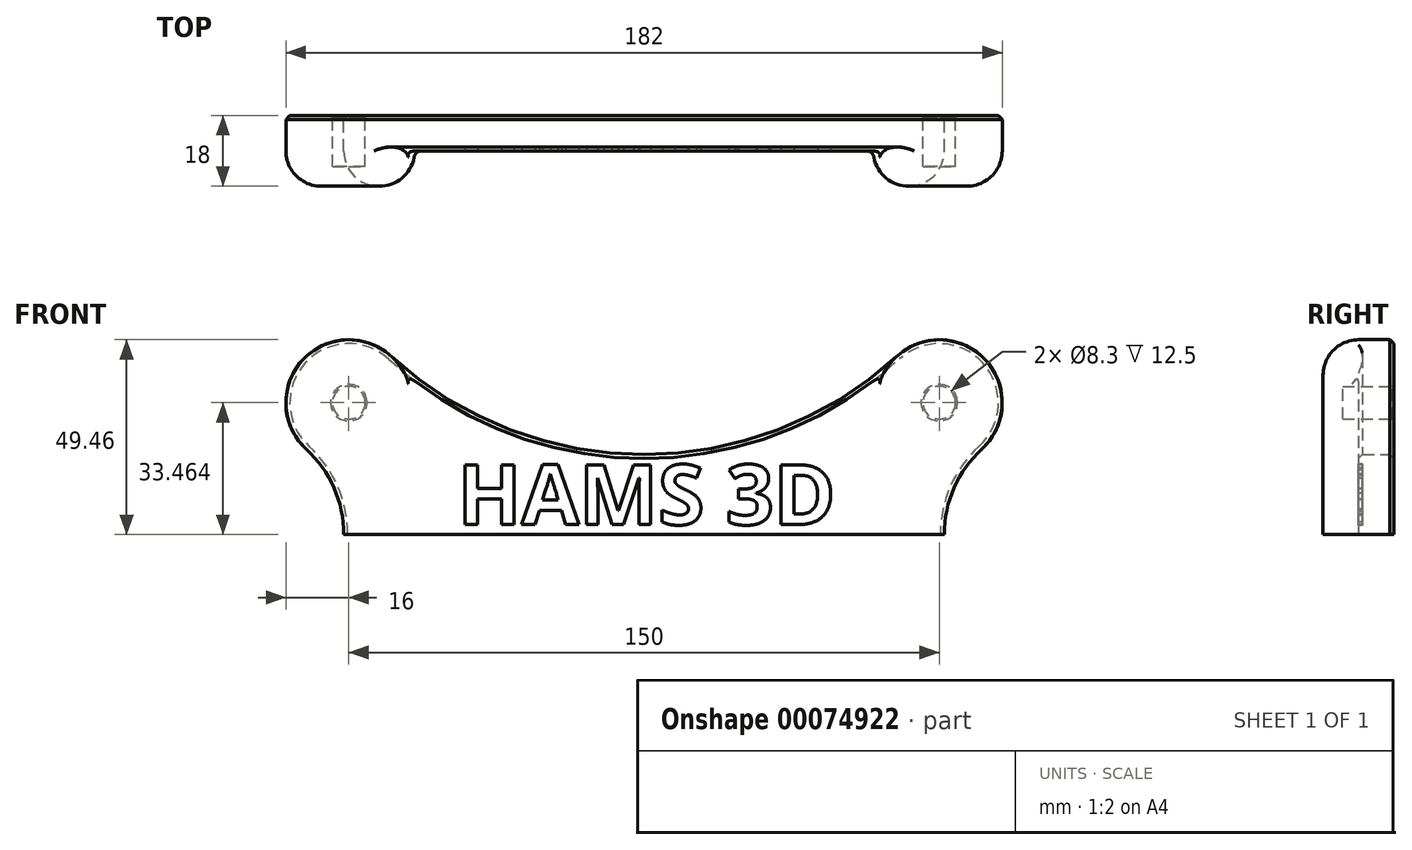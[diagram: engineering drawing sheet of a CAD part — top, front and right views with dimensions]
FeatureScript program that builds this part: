
annotation { "Feature Type Name" : "Feature", "Feature Type Description" : "" }
export const myFeature = defineFeature(function(context is Context, id is Id, definition is map)
    precondition{}
    {
        {
            assignVariable(context, id + "F0", {"name" : "mm", "anyValue" : 18});
        }
        {
            assignVariable(context, id + "F1", {"name" : "plate_thickness", "anyValue" : getVariable(context, 'mm') / 2});
        }
        {
            assignVariable(context, id + "F2", {"name" : "extra_depth", "anyValue" : 6});
        }
        {
            var Q0;
            Q0=qCreatedBy(makeId("Front.planeOp"),FACE);
            var sketch = newSketch(context, id + "F3", { "sketchPlane" : qUnion([Q0])});
            skCircle(sketch, "E0", {"center": v(0, 85) * mm, "radius": 80 * mm, "construction": true});
            skCircle(sketch, "E1", {"center": v(-75, 33.46) * mm, "radius": 11 * mm, "construction": true});
            skCircle(sketch, "E2.MirrorC", {"center": v(75, 33.46) * mm, "radius": 11 * mm, "construction": true});
            skCircle(sketch, "E3", {"center": v(-75, 33.46) * mm, "radius": 4.15 * mm});
            skCircle(sketch, "E4.MirrorC", {"center": v(75, 33.46) * mm, "radius": 4.15 * mm});
            skCircle(sketch, "E5", {"center": v(0, 115.3) * mm, "radius": 100 * mm, "construction": true});
            skArc(sketch, "E6", {"start": v(-64.19, 45.26) * mm, "mid": v(-86.8, 44.27) * mm, "end": v(-85.81, 21.67) * mm});
            skArc(sketch, "E7", {"start": v(-64.19, 45.26) * mm, "mid": v(-34.44, 26.75) * mm, "end": v(0, 20.3) * mm});
            skLineSegment(sketch, "E8", {"start": v(0, 0) * mm, "end": v(0, 115.3) * mm, "construction": true});
            skArc(sketch, "E9", {"start": v(-76.28, 0) * mm, "mid": v(-78.77, 11.84) * mm, "end": v(-85.81, 21.67) * mm});
            skArc(sketch, "E10.MirrorCS", {"start": v(64.19, 45.26) * mm, "mid": v(34.44, 26.75) * mm, "end": v(0, 20.3) * mm});
            skArc(sketch, "E11.MirrorCS", {"start": v(64.19, 45.26) * mm, "mid": v(86.8, 44.27) * mm, "end": v(85.81, 21.67) * mm});
            skArc(sketch, "E12.MirrorCS", {"start": v(76.28, 0) * mm, "mid": v(78.77, 11.84) * mm, "end": v(85.81, 21.67) * mm});
            skLineSegment(sketch, "E13", {"start": v(64.19, 45.26) * mm, "end": v(85.81, 21.67) * mm, "construction": true});
            skLineSegment(sketch, "E14", {"start": v(-76.28, 0) * mm, "end": v(76.28, 0) * mm});
            skSolve(sketch);
        }
        {
            var Q0;
            Q0=makeQuery(id+"F3.imprint","IMPRINT",FACE,{"disambiguationData":[TD([[makeQuery(id+"F3.imprint","IMPRINT",EDGE,{"derivedFrom":sQuery(id+"F3.wireOp",EDGE,"E3")}),-1.0]])]});
            extrude(context, id + "F4", {"entities" : qUnion([Q0]), "depth" : (getVariable(context, 'plate_thickness')) * mm});
        }
        {
            var Q0;
            Q0=makeQuery(id+"F4.opExtrude","CAP_FACE",FACE,{"disambiguationData":[OSD([sQuery(id+"F3.wireOp",EDGE,"E3"),sQuery(id+"F3.wireOp",EDGE,"E4.MirrorC"),sQuery(id+"F3.wireOp",EDGE,"E6"),sQuery(id+"F3.wireOp",EDGE,"E7"),sQuery(id+"F3.wireOp",EDGE,"E9"),sQuery(id+"F3.wireOp",EDGE,"E10.MirrorCS"),sQuery(id+"F3.wireOp",EDGE,"E11.MirrorCS"),sQuery(id+"F3.wireOp",EDGE,"E12.MirrorCS"),sQuery(id+"F3.wireOp",EDGE,"TTMsOwHl-O39Y-m9vk-rcTo-MJVGTNJjU1Cu")])],"isStart":false});
            var sketch = newSketch(context, id + "F5", { "sketchPlane" : qUnion([Q0])});
            skArc(sketch, "E15", {"start": v(-59.01, 34.15) * mm, "mid": v(-81.76, 47.97) * mm, "end": v(-85.81, 21.67) * mm});
            skText(sketch, "E16", { "text": "HAMS 3D", "fontName": "OpenSans-Bold.ttf"});
            skLineSegment(sketch, "E17", {"start": v(0, 17.8) * mm, "end": v(0, 20.3) * mm, "construction": true});
            skLineSegment(sketch, "E18", {"start": v(0, 2.5) * mm, "end": v(0, 0) * mm, "construction": true});
            skArc(sketch, "E19.0", {"start": v(-76.28, 0) * mm, "mid": v(-78.77, 11.84) * mm, "end": v(-85.81, 21.67) * mm});
            skLineSegment(sketch, "E20", {"start": v(-76.28, 0) * mm, "end": v(-58.28, 0) * mm});
            skArc(sketch, "E21", {"start": v(-58.28, 0) * mm, "mid": v(-58.46, 17.08) * mm, "end": v(-59.01, 34.15) * mm});
            skArc(sketch, "E22.MirrorCS", {"start": v(76.28, 0) * mm, "mid": v(78.77, 11.84) * mm, "end": v(85.81, 21.67) * mm});
            skArc(sketch, "E23.MirrorCS", {"start": v(59.01, 34.15) * mm, "mid": v(81.76, 47.97) * mm, "end": v(85.81, 21.67) * mm});
            skArc(sketch, "E24.MirrorCS", {"start": v(58.28, 0) * mm, "mid": v(58.46, 17.08) * mm, "end": v(59.01, 34.15) * mm});
            skLineSegment(sketch, "E25.MirrorCS", {"start": v(76.28, 0) * mm, "end": v(58.28, 0) * mm});
            const initialGuessF5  = {"E16": [-0.04738, 0.0025, 1, 0, 0.0153]};
            skSetInitialGuess(sketch, initialGuessF5);
            skSolve(sketch);
        }
        {
            var Q0;
            Q0=makeQuery(id+"F5.imprint","IMPRINT",FACE,{"disambiguationData":[TD([[makeQuery(id+"F5.imprint","IMPRINT",EDGE,{"derivedFrom":makeQuery(id+"F4.opExtrude","CAP_EDGE",EDGE,{"disambiguationData":[OSD([sQuery(id+"F3.wireOp",EDGE,"E3")])],"isStart":false})}),-1.0]])]});
            var Q1;
            Q1=makeQuery(id+"F5.imprint","IMPRINT",FACE,{"disambiguationData":[TD([[makeQuery(id+"F5.imprint","IMPRINT",EDGE,{"derivedFrom":makeQuery(id+"F4.opExtrude","CAP_EDGE",EDGE,{"disambiguationData":[OSD([sQuery(id+"F3.wireOp",EDGE,"E4.MirrorC")])],"isStart":false})}),1.0]])]});
            var Q2;
            Q2=makeQuery(id+"F5.imprint","IMPRINT",FACE,{"disambiguationData":[TD([[makeQuery(id+"F5.imprint","IMPRINT",EDGE,{"derivedFrom":makeQuery(id+"F4.opExtrude","CAP_EDGE",EDGE,{"disambiguationData":[OSD([sQuery(id+"F3.wireOp",EDGE,"E4.MirrorC")])],"isStart":false})}),-1.0]])]});
            var Q3;
            Q3=makeQuery(id+"F5.imprint","IMPRINT",FACE,{"disambiguationData":[TD([[makeQuery(id+"F5.imprint","IMPRINT",EDGE,{"derivedFrom":makeQuery(id+"F4.opExtrude","CAP_EDGE",EDGE,{"disambiguationData":[OSD([sQuery(id+"F3.wireOp",EDGE,"E3")])],"isStart":false})}),1.0]])]});
            extrude(context, id + "F6", {"entities" : qUnion([Q0, Q1, Q2, Q3]), "operationType" : NewBodyOperationType.ADD, "depth" : (getVariable(context, 'mm') / 2) * mm});
        }
        {
            var Q0;
            Q0=makeQuery(id+"F6.opExtrude","CAP_FACE",FACE,{"disambiguationData":[OSD([sQuery(id+"F5.wireOp",EDGE,"E22.MirrorCS"),sQuery(id+"F5.wireOp",EDGE,"E23.MirrorCS"),sQuery(id+"F5.wireOp",EDGE,"E24.MirrorCS"),sQuery(id+"F5.wireOp",EDGE,"E25.MirrorCS")])],"isStart":true});
            var Q1;
            Q1=makeQuery(id+"F6.opExtrude","CAP_FACE",FACE,{"disambiguationData":[OSD([sQuery(id+"F5.wireOp",EDGE,"E15"),sQuery(id+"F5.wireOp",EDGE,"E19.0"),sQuery(id+"F5.wireOp",EDGE,"E20"),sQuery(id+"F5.wireOp",EDGE,"E21")])],"isStart":true});
            extrude(context, id + "F7", {"entities" : qUnion([Q0, Q1]), "operationType" : NewBodyOperationType.REMOVE, "oppositeDirection" : true, "depth" : (getVariable(context, 'extra_depth') - 2) * mm});
        }
        {
            var Q0;
            Q0=makeQuery(id+"F4.opExtrude","CAP_EDGE",EDGE,{"disambiguationData":[OSD([sQuery(id+"F3.wireOp",EDGE,"E9")])],"isStart":true});
            chamfer(context, id + "F8", {"entities" : qUnion([Q0]), "width" : 1 * mm, "tangentPropagation" : true});
        }
        {
            var Q0;
            Q0=makeQuery(id+"F4.opExtrude","CAP_EDGE",EDGE,{"disambiguationData":[OSD([sQuery(id+"F3.wireOp",EDGE,"E4.MirrorC")])],"isStart":true});
            var Q1;
            Q1=makeQuery(id+"F4.opExtrude","CAP_EDGE",EDGE,{"disambiguationData":[OSD([sQuery(id+"F3.wireOp",EDGE,"E3")])],"isStart":true});
            chamfer(context, id + "F9", {"entities" : qUnion([Q0, Q1]), "width" : 0.5 * mm, "tangentPropagation" : true});
        }
        {
            var Q0;
            Q0=makeQuery(id+"F5.imprint","IMPRINT",FACE,{"disambiguationData":[TD([[makeQuery(id+"F5.imprint","IMPRINT",EDGE,{"derivedFrom":sQuery(id+"F5.wireOp",EDGE,"E16.sketch_text.stroke-0")}),-1.0]])]});
            var Q1;
            Q1=makeQuery(id+"F5.imprint","IMPRINT",FACE,{"disambiguationData":[TD([[makeQuery(id+"F5.imprint","IMPRINT",EDGE,{"derivedFrom":sQuery(id+"F5.wireOp",EDGE,"E16.sketch_text.stroke-12")}),-1.0]])]});
            var Q2;
            Q2=makeQuery(id+"F5.imprint","IMPRINT",FACE,{"disambiguationData":[TD([[makeQuery(id+"F5.imprint","IMPRINT",EDGE,{"derivedFrom":sQuery(id+"F5.wireOp",EDGE,"E16.sketch_text.stroke-24")}),-1.0]])]});
            var Q3;
            Q3=makeQuery(id+"F5.imprint","IMPRINT",FACE,{"disambiguationData":[TD([[makeQuery(id+"F5.imprint","IMPRINT",EDGE,{"derivedFrom":sQuery(id+"F5.wireOp",EDGE,"E16.sketch_text.stroke-43")}),-1.0]])]});
            var Q4;
            Q4=makeQuery(id+"F5.imprint","IMPRINT",FACE,{"disambiguationData":[TD([[makeQuery(id+"F5.imprint","IMPRINT",EDGE,{"derivedFrom":sQuery(id+"F5.wireOp",EDGE,"E16.sketch_text.stroke-71")}),-1.0]])]});
            var Q5;
            Q5=makeQuery(id+"F5.imprint","IMPRINT",FACE,{"disambiguationData":[TD([[makeQuery(id+"F5.imprint","IMPRINT",EDGE,{"derivedFrom":sQuery(id+"F5.wireOp",EDGE,"E16.sketch_text.stroke-98")}),-1.0]])]});
            extrude(context, id + "F10", {"entities" : qUnion([Q0, Q1, Q2, Q3, Q4, Q5]), "operationType" : NewBodyOperationType.REMOVE, "oppositeDirection" : true, "depth" : 1 * mm});
        }
        {
            var Q0;
            Q0=makeQuery(id+"F6.opExtrude","CAP_EDGE",EDGE,{"disambiguationData":[OSD([sQuery(id+"F5.wireOp",EDGE,"E21")])],"isStart":false});
            var Q1;
            Q1=makeQuery(id+"F6.opExtrude","CAP_EDGE",EDGE,{"disambiguationData":[OSD([sQuery(id+"F5.wireOp",EDGE,"E24.MirrorCS")])],"isStart":false});
            fillet(context, id + "F11", {"entities" : qUnion([Q0, Q1]), "radius" : (getVariable(context, 'mm') / 2) * mm, "tangentPropagation" : true, "allowEdgeOverflow" : false});
        }
        {
            var Q0;
            Q0=makeQuery(id+"F4.opExtrude","CAP_EDGE",EDGE,{"disambiguationData":[OSD([sQuery(id+"F3.wireOp",EDGE,"E7"),sQuery(id+"F3.wireOp",EDGE,"E10.MirrorCS")])],"isStart":false});
            chamfer(context, id + "F12", {"entities" : qUnion([Q0]), "width" : 1 * mm, "tangentPropagation" : true});
        }
        {
            var Q0;
            {var subQ0=sQuery(id+"F3.wireOp",EDGE,"E11.MirrorCS");var subQ1=sQuery(id+"F3.wireOp",EDGE,"E10.MirrorCS");var subQ2=sQuery(id+"F3.wireOp",EDGE,"E7");var subQ3=sQuery(id+"F5.wireOp",EDGE,"E21");var subQ4=sQuery(id+"F3.wireOp",EDGE,"E6");var subQ5=sQuery(id+"F3.wireOp",EDGE,"E14");Q0=makeQuery(id+"F11.opFillet","BLEND_EDGE",EDGE,{"blendedFrom":[makeQuery(id+"F6.opExtrude","CAP_EDGE",EDGE,{"disambiguationData":[OSD([subQ3])],"isStart":false}),makeQuery(id+"F10.boolean.opBoolean","SPLIT",FACE,{"disambiguationData":[TD([makeQuery(id+"F4.opExtrude","SWEPT_FACE",FACE,{"disambiguationData":[OSD([subQ4])]})])],"derivedFrom":makeQuery(id+"F4.opExtrude","CAP_FACE",FACE,{"disambiguationData":[OSD([sQuery(id+"F3.wireOp",EDGE,"E3"),sQuery(id+"F3.wireOp",EDGE,"E4.MirrorC"),subQ4,subQ2,sQuery(id+"F3.wireOp",EDGE,"E9"),subQ1,subQ0,sQuery(id+"F3.wireOp",EDGE,"E12.MirrorCS"),subQ5])],"isStart":false})})],"blendedInto":[makeQuery(id+"F10.boolean.opBoolean","SPLIT",FACE,{"disambiguationData":[TD([makeQuery(id+"F4.opExtrude","SWEPT_FACE",FACE,{"disambiguationData":[OSD([subQ4])]})])],"derivedFrom":makeQuery(id+"F4.opExtrude","CAP_FACE",FACE,{"disambiguationData":[OSD([sQuery(id+"F3.wireOp",EDGE,"E3"),sQuery(id+"F3.wireOp",EDGE,"E4.MirrorC"),subQ4,subQ2,sQuery(id+"F3.wireOp",EDGE,"E9"),subQ1,subQ0,sQuery(id+"F3.wireOp",EDGE,"E12.MirrorCS"),subQ5])],"isStart":false})})]});}
            var Q1;
            {var subQ0=sQuery(id+"F3.wireOp",EDGE,"E11.MirrorCS");var subQ1=sQuery(id+"F5.wireOp",EDGE,"E24.MirrorCS");var subQ2=sQuery(id+"F3.wireOp",EDGE,"E10.MirrorCS");var subQ3=sQuery(id+"F3.wireOp",EDGE,"E7");var subQ4=sQuery(id+"F3.wireOp",EDGE,"E6");var subQ5=sQuery(id+"F3.wireOp",EDGE,"E14");Q1=makeQuery(id+"F11.opFillet","BLEND_EDGE",EDGE,{"blendedFrom":[makeQuery(id+"F6.opExtrude","CAP_EDGE",EDGE,{"disambiguationData":[OSD([subQ1])],"isStart":false}),makeQuery(id+"F10.boolean.opBoolean","SPLIT",FACE,{"disambiguationData":[TD([makeQuery(id+"F4.opExtrude","SWEPT_FACE",FACE,{"disambiguationData":[OSD([subQ4])]})])],"derivedFrom":makeQuery(id+"F4.opExtrude","CAP_FACE",FACE,{"disambiguationData":[OSD([sQuery(id+"F3.wireOp",EDGE,"E3"),sQuery(id+"F3.wireOp",EDGE,"E4.MirrorC"),subQ4,subQ3,sQuery(id+"F3.wireOp",EDGE,"E9"),subQ2,subQ0,sQuery(id+"F3.wireOp",EDGE,"E12.MirrorCS"),subQ5])],"isStart":false})})],"blendedInto":[makeQuery(id+"F10.boolean.opBoolean","SPLIT",FACE,{"disambiguationData":[TD([makeQuery(id+"F4.opExtrude","SWEPT_FACE",FACE,{"disambiguationData":[OSD([subQ4])]})])],"derivedFrom":makeQuery(id+"F4.opExtrude","CAP_FACE",FACE,{"disambiguationData":[OSD([sQuery(id+"F3.wireOp",EDGE,"E3"),sQuery(id+"F3.wireOp",EDGE,"E4.MirrorC"),subQ4,subQ3,sQuery(id+"F3.wireOp",EDGE,"E9"),subQ2,subQ0,sQuery(id+"F3.wireOp",EDGE,"E12.MirrorCS"),subQ5])],"isStart":false})})]});}
            fillet(context, id + "F13", {"entities" : qUnion([Q0, Q1]), "radius" : 2 * mm, "tangentPropagation" : true, "allowEdgeOverflow" : false});
        }
    });
